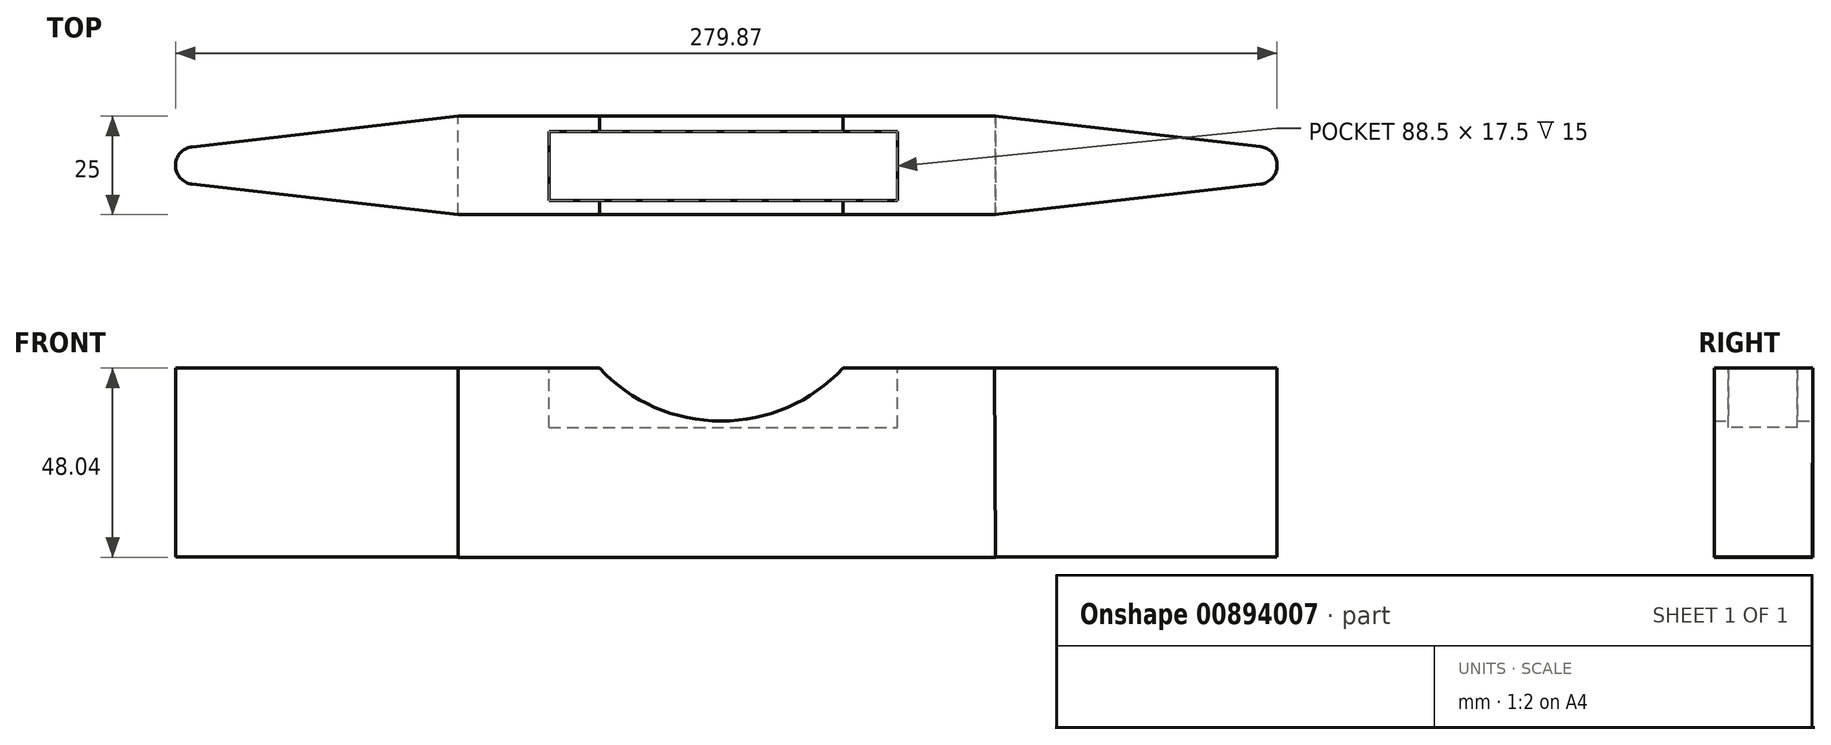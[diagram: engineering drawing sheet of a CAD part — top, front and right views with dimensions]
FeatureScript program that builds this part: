
annotation { "Feature Type Name" : "Feature", "Feature Type Description" : "" }
export const myFeature = defineFeature(function(context is Context, id is Id, definition is map)
    precondition{}
    {
        {
            var Q0;
            Q0=qCreatedBy(makeId("Front.planeOp"),FACE);
            var sketch = newSketch(context, id + "F0", { "sketchPlane" : qUnion([Q0])});
            skLineSegment(sketch, "E0", {"start": v(-67.86, 15.34) * mm, "end": v(-67.86, -32.7) * mm});
            skLineSegment(sketch, "E1", {"start": v(-67.86, -32.7) * mm, "end": v(68.72, -32.7) * mm});
            skLineSegment(sketch, "E2", {"start": v(68.44, 15.34) * mm, "end": v(68.72, -32.7) * mm});
            skLineSegment(sketch, "E3", {"start": v(68.44, 15.34) * mm, "end": v(29.95, 15.34) * mm});
            skArc(sketch, "E4", {"start": v(-31.98, 15.34) * mm, "mid": v(-1.01, 1.9) * mm, "end": v(29.95, 15.34) * mm});
            skLineSegment(sketch, "E5.trimOffspring", {"start": v(-31.98, 15.34) * mm, "end": v(-67.86, 15.34) * mm});
            skSolve(sketch);
        }
        {
            var Q0;
            Q0 = qSketchRegion(id + "F0", true);
            extrude(context, id + "F1", {"entities" : qUnion([Q0]), "depth" : 25 * mm, "offsetDistance" : 25 * mm});
        }
        {
            var Q0;
            Q0=makeQuery(id+"F1.opExtrude","SWEPT_FACE",FACE,{"disambiguationData":[OSD([sQuery(id+"F0.wireOp",EDGE,"E5.trimOffspring")])]});
            var sketch = newSketch(context, id + "F2", { "sketchPlane" : qUnion([Q0])});
            skCircle(sketch, "E6", {"center": v(-134.87, -12.5) * mm, "radius": 4.78 * mm});
            skPoint(sketch, "E6.centerSnap0", {"position": v(-67.86, -12.5) * mm});
            skLineSegment(sketch, "E7", {"start": v(-67.86, 0) * mm, "end": v(-135.41, -7.76) * mm});
            skLineSegment(sketch, "E8", {"start": v(-67.86, -25) * mm, "end": v(-135.41, -17.24) * mm});
            skSolve(sketch);
        }
        {
            var Q0;
            Q0 = qSketchRegion(id + "F2", true);
            var Q1;
            {var subQ0=sQuery(id+"F2.wireOp",EDGE,"E7");Q1=makeQuery(id+"F2.imprint","IMPRINT",FACE,{"disambiguationData":[TD([[makeQuery(id+"F2.imprint","IMPRINT",EDGE,{"derivedFrom":subQ0}),1.0]])]});}
            extrude(context, id + "F3", {"entities" : qUnion([Q0, Q1]), "operationType" : NewBodyOperationType.ADD, "oppositeDirection" : true, "depth" : 48 * mm, "offsetDistance" : 25 * mm});
        }
        {
            var Q0;
            Q0=makeQuery(id+"F1.opExtrude","SWEPT_FACE",FACE,{"disambiguationData":[OSD([sQuery(id+"F0.wireOp",EDGE,"E3")])]});
            var sketch = newSketch(context, id + "F4", { "sketchPlane" : qUnion([Q0])});
            skCircle(sketch, "E9", {"center": v(135.45, -12.5) * mm, "radius": 4.78 * mm});
            skPoint(sketch, "E9.centerSnap0", {"position": v(68.44, -12.5) * mm});
            skLineSegment(sketch, "E10", {"start": v(68.44, 0) * mm, "end": v(136, -7.75) * mm});
            skLineSegment(sketch, "E11", {"start": v(68.44, -25) * mm, "end": v(136, -17.25) * mm});
            skSolve(sketch);
        }
        {
            var Q0;
            Q0 = qSketchRegion(id + "F4", true);
            var Q1;
            {var subQ0=sQuery(id+"F4.wireOp",EDGE,"E10");Q1=makeQuery(id+"F4.imprint","IMPRINT",FACE,{"disambiguationData":[TD([[makeQuery(id+"F4.imprint","IMPRINT",EDGE,{"derivedFrom":subQ0}),-1.0]])]});}
            extrude(context, id + "F5", {"entities" : qUnion([Q0, Q1]), "operationType" : NewBodyOperationType.ADD, "oppositeDirection" : true, "depth" : 48 * mm, "offsetDistance" : 25 * mm});
        }
        {
            var Q0;
            {var subQ0=sQuery(id+"F0.wireOp",EDGE,"E5.trimOffspring");Q0=makeQuery(id+"F3.boolean.opBoolean","MERGE",FACE,{"derivedFrom":[makeQuery(id+"F1.opExtrude","SWEPT_FACE",FACE,{"disambiguationData":[OSD([subQ0])]}),makeQuery(id+"F3.opExtrude","CAP_FACE",FACE,{"disambiguationData":[OSD([sQuery(id+"F0.wireOp",EDGE,"E0"),subQ0,sQuery(id+"F2.wireOp",EDGE,"E6"),sQuery(id+"F2.wireOp",EDGE,"E7"),sQuery(id+"F2.wireOp",EDGE,"E8")])],"isStart":true})]});}
            var sketch = newSketch(context, id + "F6", { "sketchPlane" : qUnion([Q0])});
            skLineSegment(sketch, "E12.bottom", {"start": v(-44.79, -3.9) * mm, "end": v(43.71, -3.9) * mm});
            skLineSegment(sketch, "E12.top", {"start": v(-44.79, -21.4) * mm, "end": v(43.71, -21.4) * mm});
            skLineSegment(sketch, "E12.left", {"start": v(-44.79, -3.9) * mm, "end": v(-44.79, -21.4) * mm});
            skLineSegment(sketch, "E12.right", {"start": v(43.71, -3.9) * mm, "end": v(43.71, -21.4) * mm});
            skSolve(sketch);
        }
        {
            var Q0;
            Q0 = qSketchRegion(id + "F6", true);
            extrude(context, id + "F7", {"entities" : qUnion([Q0]), "operationType" : NewBodyOperationType.REMOVE, "oppositeDirection" : true, "depth" : 15 * mm, "offsetDistance" : 25 * mm});
        }
    });
